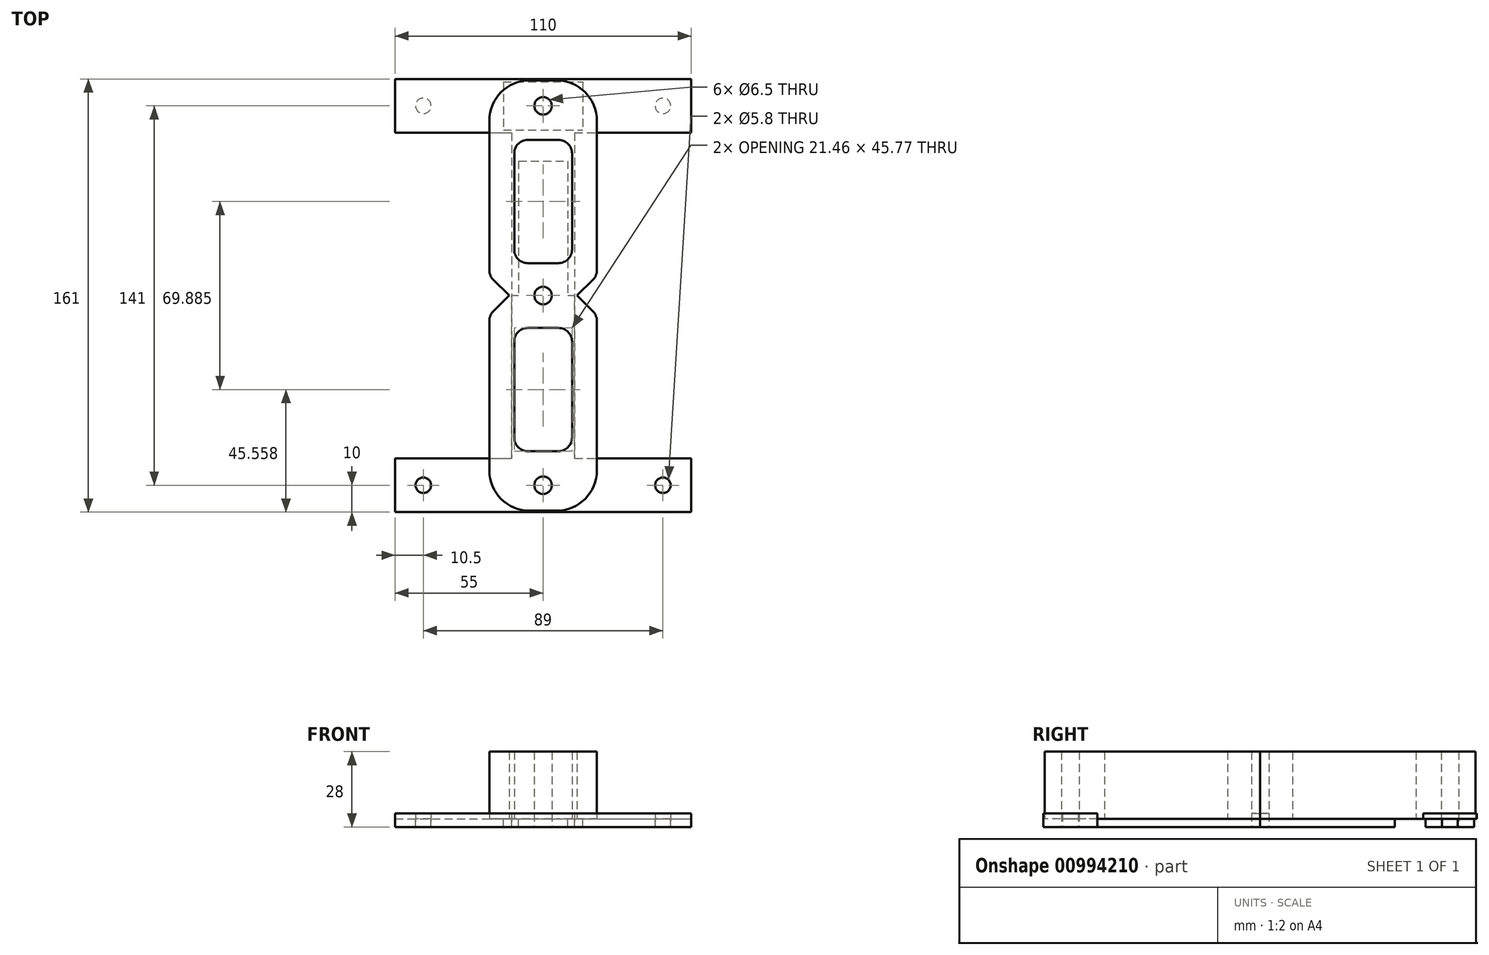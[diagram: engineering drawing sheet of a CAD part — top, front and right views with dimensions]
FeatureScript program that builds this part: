
annotation { "Feature Type Name" : "Feature", "Feature Type Description" : "" }
export const myFeature = defineFeature(function(context is Context, id is Id, definition is map)
    precondition{}
    {
        {
            var Q0;
            Q0=qCreatedBy(makeId("Top.planeOp"),FACE);
            var sketch = newSketch(context, id + "F0", { "sketchPlane" : qUnion([Q0])});
            skLineSegment(sketch, "E0.bottom", {"start": v(-55, 80.5) * mm, "end": v(55, 80.5) * mm});
            skLineSegment(sketch, "E0.top", {"start": v(-55, 60.5) * mm, "end": v(-11.7, 60.5) * mm});
            skLineSegment(sketch, "E0.left", {"start": v(-55, 80.5) * mm, "end": v(-55, 60.5) * mm});
            skLineSegment(sketch, "E0.right", {"start": v(55, 80.5) * mm, "end": v(55, 60.5) * mm});
            skLineSegment(sketch, "E1.top", {"start": v(-11.7, 0) * mm, "end": v(11.7, 0) * mm});
            skLineSegment(sketch, "E1.left", {"start": v(-11.7, 60.5) * mm, "end": v(-11.7, 0) * mm});
            skLineSegment(sketch, "E1.right", {"start": v(11.7, 60.5) * mm, "end": v(11.7, -10) * mm});
            skLineSegment(sketch, "E2.trimOffspring", {"start": v(11.7, 60.5) * mm, "end": v(55, 60.5) * mm});
            skPoint(sketch, "E3", {"position": v(0, 80.5) * mm});
            skPoint(sketch, "E4", {"position": v(0, 0) * mm});
            skPoint(sketch, "E5", {"position": v(55, 70.5) * mm});
            skPoint(sketch, "E6", {"position": v(-55, 70.5) * mm});
            skLineSegment(sketch, "E7", {"start": v(-55, 70.5) * mm, "end": v(55, 70.5) * mm, "construction": true});
            skLineSegment(sketch, "E8", {"start": v(0, 0) * mm, "end": v(0, 80.5) * mm, "construction": true});
            skPoint(sketch, "E9", {"position": v(-44.5, 70.5) * mm});
            skPoint(sketch, "E10", {"position": v(44.5, 70.5) * mm});
            skLineSegment(sketch, "E11", {"start": v(-44.5, 73.6) * mm, "end": v(44.5, 73.6) * mm, "construction": true});
            skPoint(sketch, "E12", {"position": v(0, 73.6) * mm});
            skCircle(sketch, "E13", {"center": v(-44.5, 70.5) * mm, "radius": 2.9 * mm});
            skCircle(sketch, "E14", {"center": v(44.5, 70.5) * mm, "radius": 2.9 * mm});
            skCircle(sketch, "E15.MirrorC", {"center": v(-44.5, -70.5) * mm, "radius": 2.9 * mm});
            skCircle(sketch, "E16.MirrorC", {"center": v(44.5, -70.5) * mm, "radius": 2.9 * mm});
            skLineSegment(sketch, "E17.MirrorCS", {"start": v(-55, -80.5) * mm, "end": v(-55, -60.5) * mm});
            skPoint(sketch, "E18.MirrorP", {"position": v(0, -73.6) * mm});
            skPoint(sketch, "E19.MirrorP", {"position": v(55, -70.5) * mm});
            skPoint(sketch, "E20.MirrorP", {"position": v(0, -80.5) * mm});
            skLineSegment(sketch, "E21.MirrorCS", {"start": v(-55, -80.5) * mm, "end": v(55, -80.5) * mm});
            skLineSegment(sketch, "E22.MirrorCS", {"start": v(11.7, -60.5) * mm, "end": v(55, -60.5) * mm});
            skPoint(sketch, "E23.MirrorP", {"position": v(-55, -70.5) * mm});
            skLineSegment(sketch, "E24.MirrorCS", {"start": v(-55, -60.5) * mm, "end": v(-11.7, -60.5) * mm});
            skLineSegment(sketch, "E25.MirrorCS", {"start": v(55, -80.5) * mm, "end": v(55, -60.5) * mm});
            skLineSegment(sketch, "E26.MirrorCS", {"start": v(-55, -70.5) * mm, "end": v(55, -70.5) * mm, "construction": true});
            skLineSegment(sketch, "E27.MirrorCS", {"start": v(-44.5, -73.6) * mm, "end": v(44.5, -73.6) * mm, "construction": true});
            skLineSegment(sketch, "E28.MirrorCS", {"start": v(11.7, -60.5) * mm, "end": v(11.7, -10) * mm});
            skLineSegment(sketch, "E29.MirrorCS", {"start": v(-11.7, -60.5) * mm, "end": v(-11.7, 0) * mm});
            skPoint(sketch, "E30", {"position": v(0, 70.5) * mm});
            skLineSegment(sketch, "E31.bottom", {"start": v(-14.75, 79.5) * mm, "end": v(14.75, 79.5) * mm});
            skLineSegment(sketch, "E31.top", {"start": v(-14.75, 61.5) * mm, "end": v(14.75, 61.5) * mm});
            skLineSegment(sketch, "E31.left", {"start": v(-14.75, 79.5) * mm, "end": v(-14.75, 61.5) * mm});
            skLineSegment(sketch, "E31.right", {"start": v(14.75, 79.5) * mm, "end": v(14.75, 61.5) * mm});
            skPoint(sketch, "E32", {"position": v(14.75, 70.5) * mm});
            skPoint(sketch, "E33", {"position": v(0, 79.5) * mm});
            skPoint(sketch, "E34", {"position": v(0, 61.5) * mm});
            skCircle(sketch, "E35", {"center": v(0, 70.5) * mm, "radius": 3.25 * mm});
            skLineSegment(sketch, "E36.MirrorCS", {"start": v(14.75, -79.5) * mm, "end": v(14.75, -61.5) * mm});
            skCircle(sketch, "E37.MirrorC", {"center": v(0, -70.5) * mm, "radius": 3.25 * mm});
            skPoint(sketch, "E38.MirrorP", {"position": v(0, -79.5) * mm});
            skPoint(sketch, "E39.MirrorP", {"position": v(14.75, -70.5) * mm});
            skLineSegment(sketch, "E40.MirrorCS", {"start": v(-14.75, -79.5) * mm, "end": v(14.75, -79.5) * mm});
            skLineSegment(sketch, "E41.MirrorCS", {"start": v(-14.75, -61.5) * mm, "end": v(14.75, -61.5) * mm});
            skLineSegment(sketch, "E42.MirrorCS", {"start": v(-14.75, -79.5) * mm, "end": v(-14.75, -61.5) * mm});
            skPoint(sketch, "E43.MirrorP", {"position": v(0, -61.5) * mm});
            skLineSegment(sketch, "E44.bottom", {"start": v(-9.15, 50) * mm, "end": v(9.15, 50) * mm});
            skLineSegment(sketch, "E44.top", {"start": v(-9.15, -50) * mm, "end": v(9.15, -50) * mm});
            skLineSegment(sketch, "E44.left", {"start": v(-9.15, 50) * mm, "end": v(-9.15, -50) * mm});
            skLineSegment(sketch, "E44.right", {"start": v(9.15, 50) * mm, "end": v(9.15, -50) * mm});
            skPoint(sketch, "E45", {"position": v(0, 50) * mm});
            skPoint(sketch, "E46", {"position": v(9.15, 0) * mm});
            skCircle(sketch, "E47", {"center": v(0, 0) * mm, "radius": 3.25 * mm});
            skSolve(sketch);
        }
        {
            var Q0;
            Q0 = qSketchRegion(id + "F0", true);
            var Q1;
            Q1=makeQuery(id+"F0.imprint","IMPRINT",FACE,{"disambiguationData":[TD([[makeQuery(id+"F0.imprint","IMPRINT",EDGE,{"derivedFrom":sQuery(id+"F0.wireOp",EDGE,"E14")}),1.0]])]});
            var Q2;
            Q2=makeQuery(id+"F0.imprint","IMPRINT",FACE,{"disambiguationData":[TD([[makeQuery(id+"F0.imprint","IMPRINT",EDGE,{"derivedFrom":sQuery(id+"F0.wireOp",EDGE,"E13")}),1.0]])]});
            var Q3;
            Q3=makeQuery(id+"F0.imprint","IMPRINT",FACE,{"disambiguationData":[TD([[makeQuery(id+"F0.imprint","IMPRINT",EDGE,{"derivedFrom":sQuery(id+"F0.wireOp",EDGE,"E15.MirrorC")}),-1.0]])]});
            var Q4;
            Q4=makeQuery(id+"F0.imprint","IMPRINT",FACE,{"disambiguationData":[TD([[makeQuery(id+"F0.imprint","IMPRINT",EDGE,{"derivedFrom":sQuery(id+"F0.wireOp",EDGE,"E16.MirrorC")}),-1.0]])]});
            var Q5;
            Q5=makeQuery(id+"F0.imprint","IMPRINT",FACE,{"disambiguationData":[TD([[makeQuery(id+"F0.imprint","IMPRINT",EDGE,{"derivedFrom":sQuery(id+"F0.wireOp",EDGE,"E31.bottom")}),-1.0]])]});
            var Q6;
            Q6=makeQuery(id+"F0.imprint","IMPRINT",FACE,{"disambiguationData":[TD([[makeQuery(id+"F0.imprint","IMPRINT",EDGE,{"derivedFrom":sQuery(id+"F0.wireOp",EDGE,"E36.MirrorCS")}),1.0]])]});
            var Q7;
            {var subQ1=sQuery(id+"F0.wireOp",EDGE,"E44.bottom");Q7=makeQuery(id+"F0.imprint","IMPRINT",FACE,{"disambiguationData":[TD([[makeQuery(id+"F0.imprint","IMPRINT",EDGE,{"derivedFrom":subQ1}),-1.0]])]});}
            var Q8;
            {var subQ1=sQuery(id+"F0.wireOp",EDGE,"E44.top");Q8=makeQuery(id+"F0.imprint","IMPRINT",FACE,{"disambiguationData":[TD([[makeQuery(id+"F0.imprint","IMPRINT",EDGE,{"derivedFrom":subQ1}),1.0]])]});}
            var Q9;
            Q9=makeQuery(id+"F0.imprint","IMPRINT",FACE,{"disambiguationData":[TD([[makeQuery(id+"F0.imprint","IMPRINT",EDGE,{"derivedFrom":sQuery(id+"F0.wireOp",EDGE,"nzZwaja2-NtX4-x43H-yWwb-LPVIa0RzHxDo.bottom")}),-1.0]])]});
            extrude(context, id + "F1", {"entities" : qUnion([Q0, Q1, Q2, Q3, Q4, Q5, Q6, Q7, Q8, Q9]), "depth" : 2 * mm, "offsetDistance" : 25 * mm});
        }
        {
            var Q0;
            Q0=makeQuery(id+"F0.imprint","IMPRINT",FACE,{"disambiguationData":[TD([[makeQuery(id+"F0.imprint","IMPRINT",EDGE,{"derivedFrom":sQuery(id+"F0.wireOp",EDGE,"E14")}),1.0]])]});
            var Q1;
            Q1=makeQuery(id+"F0.imprint","IMPRINT",FACE,{"disambiguationData":[TD([[makeQuery(id+"F0.imprint","IMPRINT",EDGE,{"derivedFrom":sQuery(id+"F0.wireOp",EDGE,"E13")}),1.0]])]});
            var Q2;
            Q2=makeQuery(id+"F0.imprint","IMPRINT",FACE,{"disambiguationData":[TD([[makeQuery(id+"F0.imprint","IMPRINT",EDGE,{"derivedFrom":sQuery(id+"F0.wireOp",EDGE,"E16.MirrorC")}),-1.0]])]});
            var Q3;
            Q3=makeQuery(id+"F0.imprint","IMPRINT",FACE,{"disambiguationData":[TD([[makeQuery(id+"F0.imprint","IMPRINT",EDGE,{"derivedFrom":sQuery(id+"F0.wireOp",EDGE,"E15.MirrorC")}),-1.0]])]});
            var Q4;
            Q4=makeQuery(id+"F0.imprint","IMPRINT",FACE,{"disambiguationData":[TD([[makeQuery(id+"F0.imprint","IMPRINT",EDGE,{"derivedFrom":sQuery(id+"F0.wireOp",EDGE,"E31.bottom")}),-1.0]])]});
            var Q5;
            Q5=makeQuery(id+"F0.imprint","IMPRINT",FACE,{"disambiguationData":[TD([[makeQuery(id+"F0.imprint","IMPRINT",EDGE,{"derivedFrom":sQuery(id+"F0.wireOp",EDGE,"E36.MirrorCS")}),1.0]])]});
            var Q6;
            {var subQ1=sQuery(id+"F0.wireOp",EDGE,"E44.bottom");Q6=makeQuery(id+"F0.imprint","IMPRINT",FACE,{"disambiguationData":[TD([[makeQuery(id+"F0.imprint","IMPRINT",EDGE,{"derivedFrom":subQ1}),-1.0]])]});}
            var Q7;
            {var subQ1=sQuery(id+"F0.wireOp",EDGE,"E44.top");Q7=makeQuery(id+"F0.imprint","IMPRINT",FACE,{"disambiguationData":[TD([[makeQuery(id+"F0.imprint","IMPRINT",EDGE,{"derivedFrom":subQ1}),1.0]])]});}
            var Q8;
            Q8=makeQuery(id+"F0.imprint","IMPRINT",FACE,{"disambiguationData":[TD([[makeQuery(id+"F0.imprint","IMPRINT",EDGE,{"derivedFrom":sQuery(id+"F0.wireOp",EDGE,"nzZwaja2-NtX4-x43H-yWwb-LPVIa0RzHxDo.bottom")}),-1.0]])]});
            extrude(context, id + "F2", {"entities" : qUnion([Q0, Q1, Q2, Q3, Q4, Q5, Q6, Q7, Q8]), "operationType" : NewBodyOperationType.ADD, "oppositeDirection" : true, "depth" : 3 * mm, "offsetDistance" : 25 * mm});
        }
        {
            var Q0;
            Q0=qCreatedBy(makeId("Top.planeOp"),FACE);
            var sketch = newSketch(context, id + "F3", { "sketchPlane" : qUnion([Q0])});
            skPoint(sketch, "E48.0", {"position": v(0, 70.5) * mm});
            skCircle(sketch, "E49.0", {"center": v(0, 70.5) * mm, "radius": 3.25 * mm});
            skPoint(sketch, "E50.0", {"position": v(0, 0) * mm});
            skCircle(sketch, "E51.0", {"center": v(0, 0) * mm, "radius": 3.25 * mm});
            skPoint(sketch, "E52.0", {"position": v(0, -70.5) * mm});
            skCircle(sketch, "E53.0", {"center": v(0, -70.5) * mm, "radius": 3.25 * mm});
            skLineSegment(sketch, "E54.left", {"start": v(-20, 65) * mm, "end": v(-20, 9.44) * mm});
            skLineSegment(sketch, "E54.right", {"start": v(20, 65) * mm, "end": v(20, 9.44) * mm});
            skPoint(sketch, "E55", {"position": v(20, 0) * mm});
            skLineSegment(sketch, "E56", {"start": v(0, 110) * mm, "end": v(0, -80) * mm, "construction": true});
            skLineSegment(sketch, "E57", {"start": v(20, 0) * mm, "end": v(-20, 0) * mm, "construction": true});
            skLineSegment(sketch, "E58", {"start": v(12.63, 0) * mm, "end": v(18.54, 5.9) * mm});
            skLineSegment(sketch, "E59", {"start": v(12.63, 0) * mm, "end": v(18.54, -5.9) * mm});
            skPoint(sketch, "E60.MirrorP", {"position": v(-20, 0) * mm});
            skLineSegment(sketch, "E61.MirrorCS", {"start": v(-12.63, 0) * mm, "end": v(-18.54, 5.9) * mm});
            skLineSegment(sketch, "E62.MirrorCS", {"start": v(-12.63, 0) * mm, "end": v(-18.54, -5.9) * mm});
            skLineSegment(sketch, "E63.trimOffspring", {"start": v(-20, -9.44) * mm, "end": v(-20, -65) * mm});
            skLineSegment(sketch, "E64.trimOffspring", {"start": v(20, -9.44) * mm, "end": v(20, -65) * mm});
            skLineSegment(sketch, "E65.bottom", {"start": v(-5, 80) * mm, "end": v(5, 80) * mm});
            skLineSegment(sketch, "E65.top", {"start": v(-5, -80) * mm, "end": v(5, -80) * mm});
            skPoint(sketch, "E66", {"position": v(45.4, 0) * mm});
            skPoint(sketch, "E67.orphan", {"position": v(-20, -110) * mm});
            skPoint(sketch, "E68.orphan", {"position": v(20, -110) * mm});
            skPoint(sketch, "E69.orphan", {"position": v(0, -110) * mm});
            skPoint(sketch, "E70.orphan", {"position": v(45.4, 80) * mm});
            skPoint(sketch, "E71.orphan", {"position": v(45.4, -80) * mm});
            skPoint(sketch, "E72.visualSharp", {"position": v(-20, 80) * mm});
            skArc(sketch, "E72.filletArc", {"start": v(-5, 80) * mm, "mid": v(-15.6, 75.6) * mm, "end": v(-20, 65) * mm});
            skPoint(sketch, "E73.visualSharp", {"position": v(20, 80) * mm});
            skArc(sketch, "E73.filletArc", {"start": v(20, 65) * mm, "mid": v(15.6, 75.6) * mm, "end": v(5, 80) * mm});
            skPoint(sketch, "E74.visualSharp", {"position": v(-20, -80) * mm});
            skArc(sketch, "E74.filletArc", {"start": v(-20, -65) * mm, "mid": v(-15.6, -75.6) * mm, "end": v(-5, -80) * mm});
            skPoint(sketch, "E75.visualSharp", {"position": v(20, -80) * mm});
            skArc(sketch, "E75.filletArc", {"start": v(5, -80) * mm, "mid": v(15.6, -75.6) * mm, "end": v(20, -65) * mm});
            skLineSegment(sketch, "E76.bottom", {"start": v(-5.73, 57.83) * mm, "end": v(5.73, 57.83) * mm});
            skLineSegment(sketch, "E76.top", {"start": v(-5.73, 12.06) * mm, "end": v(5.73, 12.06) * mm});
            skLineSegment(sketch, "E76.left", {"start": v(-10.73, 52.83) * mm, "end": v(-10.73, 17.06) * mm});
            skLineSegment(sketch, "E76.right", {"start": v(10.73, 52.83) * mm, "end": v(10.73, 17.06) * mm});
            skPoint(sketch, "E77", {"position": v(10.73, 34.94) * mm});
            skPoint(sketch, "E78", {"position": v(0, 12.06) * mm});
            skLineSegment(sketch, "E79.MirrorCS", {"start": v(10.73, -52.83) * mm, "end": v(10.73, -17.06) * mm});
            skLineSegment(sketch, "E80.MirrorCS", {"start": v(-5.73, -12.06) * mm, "end": v(5.73, -12.06) * mm});
            skPoint(sketch, "E81.MirrorP", {"position": v(0, -12.06) * mm});
            skLineSegment(sketch, "E82.MirrorCS", {"start": v(-10.73, -52.83) * mm, "end": v(-10.73, -17.06) * mm});
            skPoint(sketch, "E83.MirrorP", {"position": v(10.73, -34.94) * mm});
            skLineSegment(sketch, "E84.MirrorCS", {"start": v(-5.73, -57.83) * mm, "end": v(5.73, -57.83) * mm});
            skPoint(sketch, "E85.visualSharp", {"position": v(10.73, 57.83) * mm});
            skArc(sketch, "E85.filletArc", {"start": v(10.73, 52.83) * mm, "mid": v(9.27, 56.36) * mm, "end": v(5.73, 57.83) * mm});
            skPoint(sketch, "E86.visualSharp", {"position": v(-10.73, 57.83) * mm});
            skArc(sketch, "E86.filletArc", {"start": v(-5.73, 57.83) * mm, "mid": v(-9.27, 56.36) * mm, "end": v(-10.73, 52.83) * mm});
            skPoint(sketch, "E87.visualSharp", {"position": v(-10.73, 12.06) * mm});
            skArc(sketch, "E87.filletArc", {"start": v(-10.73, 17.06) * mm, "mid": v(-9.27, 13.52) * mm, "end": v(-5.73, 12.06) * mm});
            skPoint(sketch, "E88.visualSharp", {"position": v(10.73, 12.06) * mm});
            skArc(sketch, "E88.filletArc", {"start": v(5.73, 12.06) * mm, "mid": v(9.27, 13.52) * mm, "end": v(10.73, 17.06) * mm});
            skPoint(sketch, "E89.visualSharp", {"position": v(-10.73, -12.06) * mm});
            skArc(sketch, "E89.filletArc", {"start": v(-5.73, -12.06) * mm, "mid": v(-9.27, -13.52) * mm, "end": v(-10.73, -17.06) * mm});
            skPoint(sketch, "E90.visualSharp", {"position": v(10.73, -12.06) * mm});
            skArc(sketch, "E90.filletArc", {"start": v(10.73, -17.06) * mm, "mid": v(9.27, -13.52) * mm, "end": v(5.73, -12.06) * mm});
            skPoint(sketch, "E91.visualSharp", {"position": v(10.73, -57.83) * mm});
            skArc(sketch, "E91.filletArc", {"start": v(5.73, -57.83) * mm, "mid": v(9.27, -56.36) * mm, "end": v(10.73, -52.83) * mm});
            skPoint(sketch, "E92.visualSharp", {"position": v(-10.73, -57.83) * mm});
            skArc(sketch, "E92.filletArc", {"start": v(-10.73, -52.83) * mm, "mid": v(-9.27, -56.36) * mm, "end": v(-5.73, -57.83) * mm});
            skPoint(sketch, "E93.visualSharp", {"position": v(-20, -7.37) * mm});
            skArc(sketch, "E93.filletArc", {"start": v(-18.54, -5.9) * mm, "mid": v(-19.62, -7.53) * mm, "end": v(-20, -9.44) * mm});
            skPoint(sketch, "E94.visualSharp", {"position": v(20, -7.37) * mm});
            skArc(sketch, "E94.filletArc", {"start": v(20, -9.44) * mm, "mid": v(19.62, -7.53) * mm, "end": v(18.54, -5.9) * mm});
            skPoint(sketch, "E95.visualSharp", {"position": v(20, 7.37) * mm});
            skArc(sketch, "E95.filletArc", {"start": v(18.54, 5.9) * mm, "mid": v(19.62, 7.53) * mm, "end": v(20, 9.44) * mm});
            skPoint(sketch, "E96.visualSharp", {"position": v(-20, 7.37) * mm});
            skArc(sketch, "E96.filletArc", {"start": v(-20, 9.44) * mm, "mid": v(-19.62, 7.53) * mm, "end": v(-18.54, 5.9) * mm});
            skSolve(sketch);
        }
        {
            var Q0;
            Q0 = qSketchRegion(id + "F3", true);
            extrude(context, id + "F4", {"entities" : qUnion([Q0]), "depth" : 25 * mm, "offsetDistance" : 25 * mm});
        }
    });
